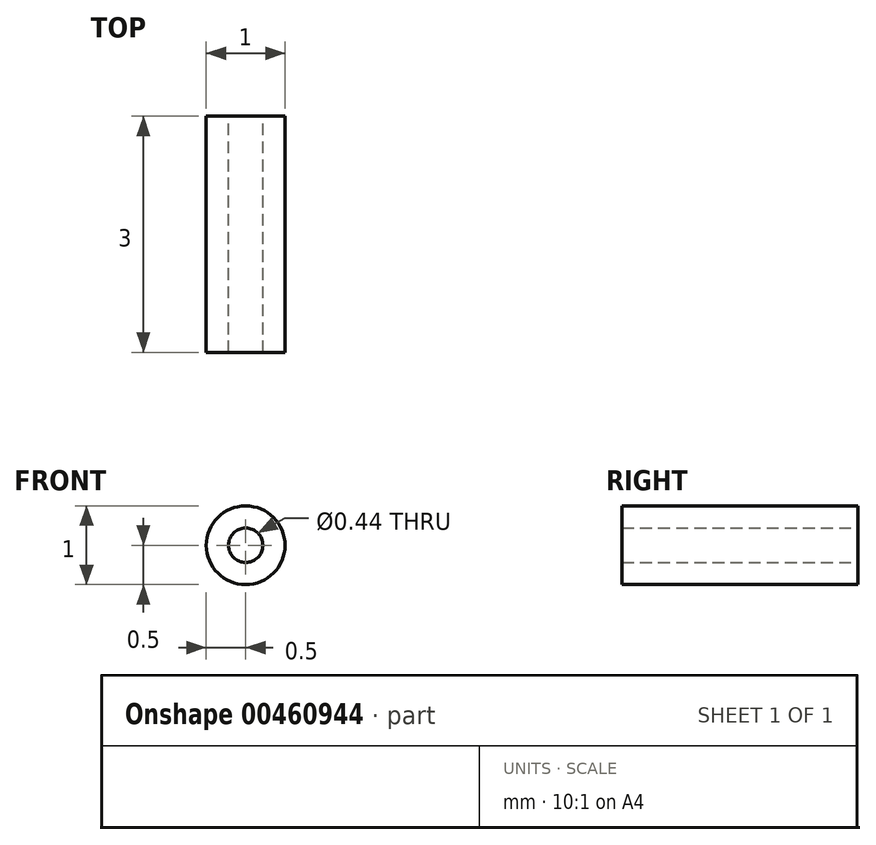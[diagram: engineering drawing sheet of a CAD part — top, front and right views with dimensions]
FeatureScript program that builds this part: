
annotation { "Feature Type Name" : "Feature", "Feature Type Description" : "" }
export const myFeature = defineFeature(function(context is Context, id is Id, definition is map)
    precondition{}
    {
        {
            var Q0;
            Q0=qCreatedBy(makeId("Front.planeOp"),FACE);
            var sketch = newSketch(context, id + "F0", { "sketchPlane" : qUnion([Q0])});
            skCircle(sketch, "E0", {"center": v(0, 0) * mm, "radius": 0.5 * mm});
            skCircle(sketch, "E1", {"center": v(0, 0) * mm, "radius": 0.22 * mm});
            skSolve(sketch);
        }
        {
            var Q0;
            Q0=makeQuery(id+"F0.imprint","IMPRINT",FACE,{"disambiguationData":[TD([[makeQuery(id+"F0.imprint","IMPRINT",EDGE,{"derivedFrom":sQuery(id+"F0.wireOp",EDGE,"E0")}),1.0]])]});
            extrude(context, id + "F1", {"entities" : qUnion([Q0]), "depth" : 3 * mm});
        }
    });
